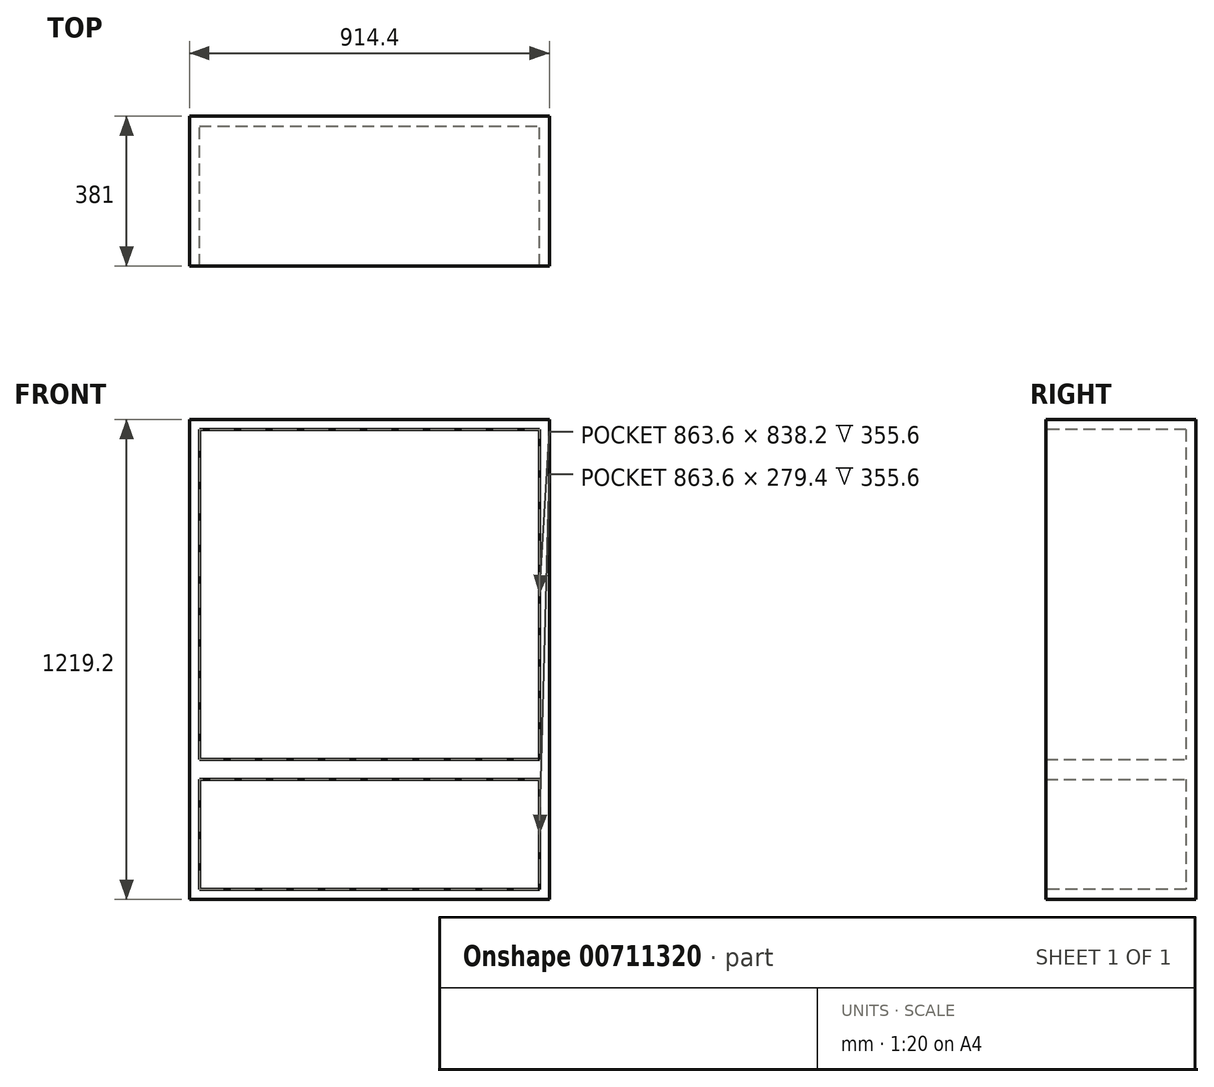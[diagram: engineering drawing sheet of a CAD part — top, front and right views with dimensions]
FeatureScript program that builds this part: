
annotation { "Feature Type Name" : "Feature", "Feature Type Description" : "" }
export const myFeature = defineFeature(function(context is Context, id is Id, definition is map)
    precondition{}
    {
        {
            var Q0;
            Q0=qCreatedBy(makeId("Top.planeOp"),FACE);
            var sketch = newSketch(context, id + "F0", { "sketchPlane" : qUnion([Q0])});
            skLineSegment(sketch, "E0.bottom", {"start": v(-326.36, -185.6) * mm, "end": v(588.04, -185.6) * mm});
            skLineSegment(sketch, "E0.top", {"start": v(-326.36, 195.4) * mm, "end": v(588.04, 195.4) * mm});
            skLineSegment(sketch, "E0.left", {"start": v(-326.36, -185.6) * mm, "end": v(-326.36, 195.4) * mm});
            skLineSegment(sketch, "E0.right", {"start": v(588.04, -185.6) * mm, "end": v(588.04, 195.4) * mm});
            skSolve(sketch);
        }
        {
            var Q0;
            Q0=makeQuery(id+"F0.imprint","IMPRINT",FACE,{"disambiguationData":[TD([[makeQuery(id+"F0.imprint","IMPRINT",EDGE,{"derivedFrom":sQuery(id+"F0.wireOp",EDGE,"E0.bottom")}),1.0]])]});
            extrude(context, id + "F1", {"entities" : qUnion([Q0]), "depth" : 1219.2 * mm, "offsetDistance" : 25 * mm});
        }
        {
            var Q0;
            Q0=makeQuery(id+"F1.opExtrude","SWEPT_FACE",FACE,{"disambiguationData":[OSD([sQuery(id+"F0.wireOp",EDGE,"E0.bottom")])]});
            var sketch = newSketch(context, id + "F2", { "sketchPlane" : qUnion([Q0])});
            skLineSegment(sketch, "E1.bottom", {"start": v(-300.96, 1193.8) * mm, "end": v(562.64, 1193.8) * mm});
            skLineSegment(sketch, "E1.top", {"start": v(-300.96, 25.4) * mm, "end": v(562.64, 25.4) * mm});
            skLineSegment(sketch, "E1.left", {"start": v(-300.96, 1193.8) * mm, "end": v(-300.96, 25.4) * mm});
            skLineSegment(sketch, "E1.right", {"start": v(562.64, 1193.8) * mm, "end": v(562.64, 25.4) * mm});
            skSolve(sketch);
        }
        {
            var Q0;
            Q0=makeQuery(id+"F2.imprint","IMPRINT",FACE,{"disambiguationData":[TD([[makeQuery(id+"F2.imprint","IMPRINT",EDGE,{"derivedFrom":sQuery(id+"F2.wireOp",EDGE,"E1.bottom")}),-1.0]])]});
            extrude(context, id + "F3", {"entities" : qUnion([Q0]), "operationType" : NewBodyOperationType.REMOVE, "oppositeDirection" : true, "depth" : 355.6 * mm, "offsetDistance" : 25 * mm});
        }
        {
            var Q0;
            Q0=makeQuery(id+"F3.boolean.opBoolean","COPY",FACE,{"derivedFrom":makeQuery(id+"F3.opExtrude","CAP_FACE",FACE,{"disambiguationData":[OSD([sQuery(id+"F2.wireOp",EDGE,"E1.bottom"),sQuery(id+"F2.wireOp",EDGE,"E1.top"),sQuery(id+"F2.wireOp",EDGE,"E1.left"),sQuery(id+"F2.wireOp",EDGE,"E1.right")])],"isStart":false})});
            var sketch = newSketch(context, id + "F4", { "sketchPlane" : qUnion([Q0])});
            skLineSegment(sketch, "E2.bottom", {"start": v(-300.96, 355.6) * mm, "end": v(562.64, 355.6) * mm});
            skLineSegment(sketch, "E2.top", {"start": v(-300.96, 304.8) * mm, "end": v(562.64, 304.8) * mm});
            skLineSegment(sketch, "E2.left", {"start": v(-300.96, 355.6) * mm, "end": v(-300.96, 304.8) * mm});
            skLineSegment(sketch, "E2.right", {"start": v(562.64, 355.6) * mm, "end": v(562.64, 304.8) * mm});
            skSolve(sketch);
        }
        {
            var Q0;
            Q0=makeQuery(id+"F4.imprint","IMPRINT",FACE,{"disambiguationData":[TD([[makeQuery(id+"F4.imprint","IMPRINT",EDGE,{"derivedFrom":sQuery(id+"F4.wireOp",EDGE,"E2.bottom")}),-1.0]])]});
            extrude(context, id + "F5", {"entities" : qUnion([Q0]), "operationType" : NewBodyOperationType.ADD, "depth" : 355.6 * mm, "offsetDistance" : 25 * mm});
        }
    });
